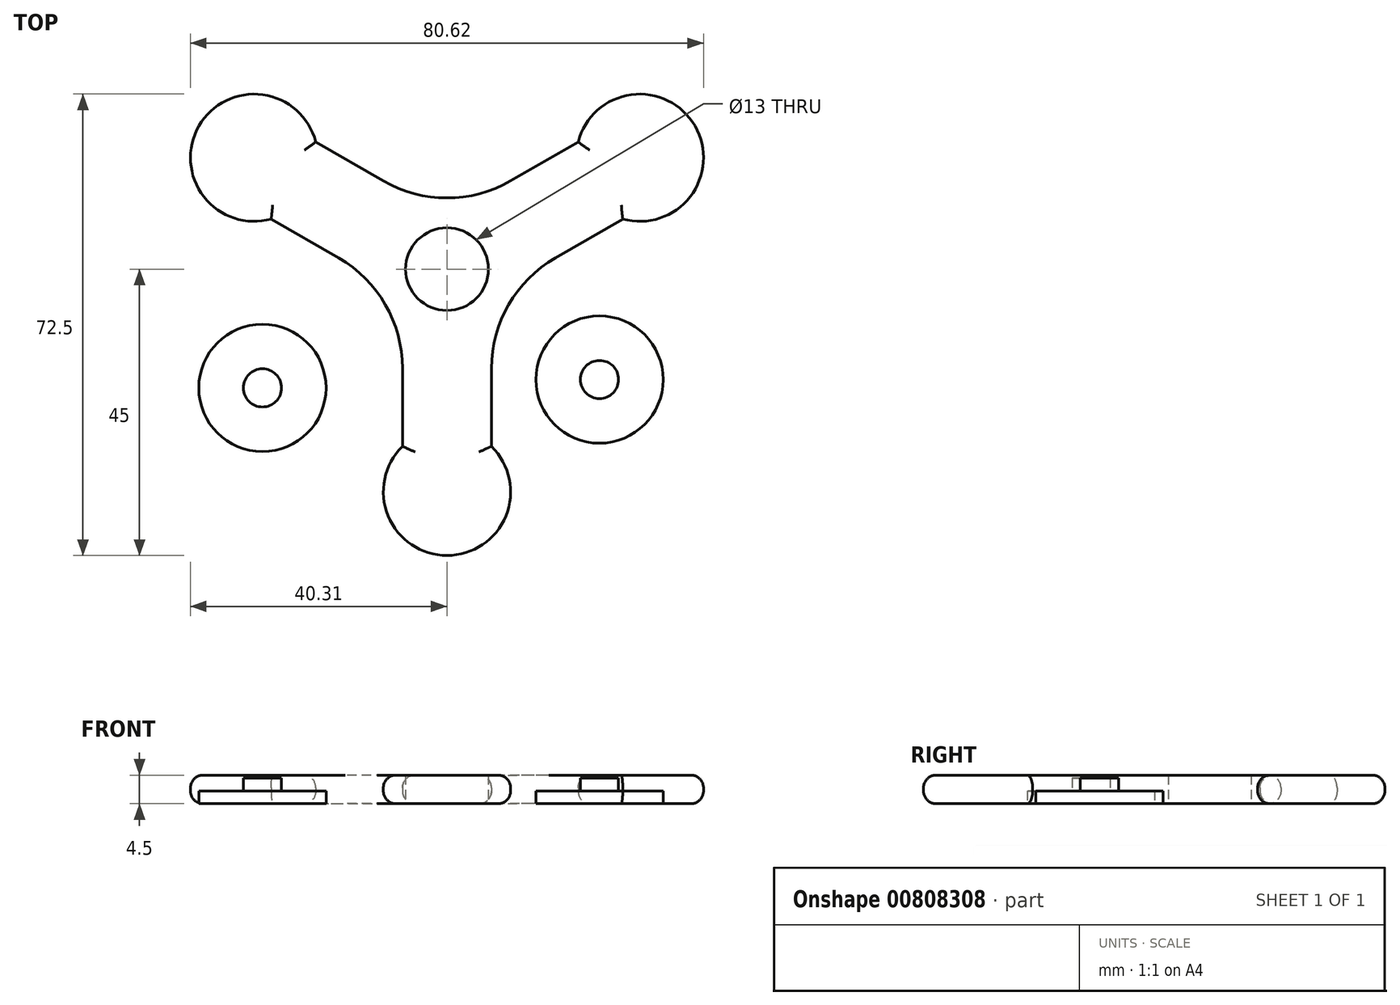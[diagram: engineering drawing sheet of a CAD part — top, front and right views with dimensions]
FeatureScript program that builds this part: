
annotation { "Feature Type Name" : "Feature", "Feature Type Description" : "" }
export const myFeature = defineFeature(function(context is Context, id is Id, definition is map)
    precondition{}
    {
        {
            var Q0;
            Q0=qCreatedBy(makeId("Top.planeOp"),FACE);
            var sketch = newSketch(context, id + "F0", { "sketchPlane" : qUnion([Q0])});
            skCircle(sketch, "E0", {"center": v(0, 0) * mm, "radius": 6.5 * mm});
            skCircle(sketch, "E1.cCircle", {"center": v(0, 0) * mm, "radius": 9.7 * mm, "construction": true});
            skLineSegment(sketch, "E1.0", {"start": v(-16.8, 9.7) * mm, "end": v(16.8, 9.7) * mm, "construction": true});
            skLineSegment(sketch, "E1.1", {"start": v(16.8, 9.7) * mm, "end": v(0, -19.4) * mm, "construction": true});
            skLineSegment(sketch, "E1.2", {"start": v(0, -19.4) * mm, "end": v(-16.8, 9.7) * mm, "construction": true});
            skPoint(sketch, "E1.0.midPoint", {"position": v(0, 9.7) * mm});
            skLineSegment(sketch, "E2", {"start": v(0, 0) * mm, "end": v(-37.72, 21.78) * mm, "construction": true});
            skLineSegment(sketch, "E3", {"start": v(0, 0) * mm, "end": v(32.3, 18.65) * mm, "construction": true});
            skLineSegment(sketch, "E4", {"start": v(0, 0) * mm, "end": v(0, -39.08) * mm, "construction": true});
            skLineSegment(sketch, "E5", {"start": v(0, 8.08) * mm, "end": v(26.1, 23.15) * mm, "construction": true});
            skLineSegment(sketch, "E6", {"start": v(-34.22, 11.67) * mm, "end": v(-7, -4.04) * mm, "construction": true});
            skLineSegment(sketch, "E7", {"start": v(-7, -4.04) * mm, "end": v(-7, -34.03) * mm, "construction": true});
            skLineSegment(sketch, "E8", {"start": v(7, -32.22) * mm, "end": v(7, -4.04) * mm, "construction": true});
            skLineSegment(sketch, "E9", {"start": v(7, -4.04) * mm, "end": v(32.17, 10.5) * mm, "construction": true});
            skLineSegment(sketch, "E10", {"start": v(0, 8.08) * mm, "end": v(-23.07, 21.4) * mm, "construction": true});
            skCircle(sketch, "E11", {"center": v(30.31, 17.5) * mm, "radius": 10 * mm});
            skCircle(sketch, "E12", {"center": v(-30.31, 17.5) * mm, "radius": 10 * mm});
            skCircle(sketch, "E13", {"center": v(0, -35) * mm, "radius": 10 * mm});
            skLineSegment(sketch, "E14", {"start": v(-27.63, 7.87) * mm, "end": v(-17, 1.73) * mm});
            skLineSegment(sketch, "E15", {"start": v(-7, -27.86) * mm, "end": v(-7, -15.59) * mm});
            skLineSegment(sketch, "E16", {"start": v(-20.63, 20) * mm, "end": v(-10, 13.86) * mm});
            skLineSegment(sketch, "E17", {"start": v(20.63, 20) * mm, "end": v(10, 13.86) * mm});
            skLineSegment(sketch, "E18", {"start": v(27.63, 7.87) * mm, "end": v(17, 1.73) * mm});
            skLineSegment(sketch, "E19", {"start": v(7, -27.86) * mm, "end": v(7, -15.59) * mm});
            skPoint(sketch, "E20.visualSharp", {"position": v(-7, -4.04) * mm});
            skArc(sketch, "E20.filletArc", {"start": v(-7, -15.59) * mm, "mid": v(-9.68, -5.59) * mm, "end": v(-17, 1.73) * mm});
            skPoint(sketch, "E21.visualSharp", {"position": v(0, 8.08) * mm});
            skArc(sketch, "E21.filletArc", {"start": v(-10, 13.86) * mm, "mid": v(0, 11.18) * mm, "end": v(10, 13.86) * mm});
            skPoint(sketch, "E22.visualSharp", {"position": v(7, -4.04) * mm});
            skArc(sketch, "E22.filletArc", {"start": v(17, 1.73) * mm, "mid": v(9.68, -5.59) * mm, "end": v(7, -15.59) * mm});
            skCircle(sketch, "E23", {"center": v(-29, -18.67) * mm, "radius": 10 * mm});
            skCircle(sketch, "E24", {"center": v(23.97, -17.36) * mm, "radius": 10 * mm});
            skSolve(sketch);
        }
        {
            var Q0;
            {var subQ0=sQuery(id+"F0.wireOp",EDGE,"E12");var subQ1=makeQuery(id+"F0.imprint","INTERSECT",VERTEX,{"derivedFrom":[subQ0,sQuery(id+"F0.wireOp",EDGE,"E14")]});Q0=makeQuery(id+"F0.imprint","IMPRINT",FACE,{"disambiguationData":[TD([[makeQuery(id+"F0.imprint","IMPRINT",EDGE,{"disambiguationData":[TD([[subQ1,1.0]])],"derivedFrom":subQ0}),1.0]])]});}
            var Q1;
            {var subQ0=sQuery(id+"F0.wireOp",EDGE,"E13");var subQ1=makeQuery(id+"F0.imprint","INTERSECT",VERTEX,{"derivedFrom":[subQ0,sQuery(id+"F0.wireOp",EDGE,"E15")]});Q1=makeQuery(id+"F0.imprint","IMPRINT",FACE,{"disambiguationData":[TD([[makeQuery(id+"F0.imprint","IMPRINT",EDGE,{"disambiguationData":[TD([[subQ1,1.0]])],"derivedFrom":subQ0}),1.0]])]});}
            var Q2;
            {var subQ0=sQuery(id+"F0.wireOp",EDGE,"E11");var subQ1=makeQuery(id+"F0.imprint","INTERSECT",VERTEX,{"derivedFrom":[subQ0,sQuery(id+"F0.wireOp",EDGE,"E17")]});Q2=makeQuery(id+"F0.imprint","IMPRINT",FACE,{"disambiguationData":[TD([[makeQuery(id+"F0.imprint","IMPRINT",EDGE,{"disambiguationData":[TD([[subQ1,-1.0]])],"derivedFrom":subQ0}),1.0]])]});}
            var Q3;
            Q3=makeQuery(id+"F0.imprint","IMPRINT",FACE,{"disambiguationData":[TD([[makeQuery(id+"F0.imprint","IMPRINT",EDGE,{"derivedFrom":sQuery(id+"F0.wireOp",EDGE,"E0")}),-1.0]])]});
            extrude(context, id + "F1", {"entities" : qUnion([Q0, Q1, Q2, Q3]), "depth" : 4.5 * mm, "offsetDistance" : 25 * mm});
        }
        {
            var Q0;
            Q0=makeQuery(id+"F1.opExtrude","CAP_EDGE",EDGE,{"disambiguationData":[OSD([sQuery(id+"F0.wireOp",EDGE,"E13")])],"isStart":false});
            var Q1;
            Q1=makeQuery(id+"F1.opExtrude","CAP_EDGE",EDGE,{"disambiguationData":[OSD([sQuery(id+"F0.wireOp",EDGE,"E19")])],"isStart":false});
            var Q2;
            Q2=makeQuery(id+"F1.opExtrude","CAP_EDGE",EDGE,{"disambiguationData":[OSD([sQuery(id+"F0.wireOp",EDGE,"E22.filletArc")])],"isStart":false});
            var Q3;
            Q3=makeQuery(id+"F1.opExtrude","CAP_EDGE",EDGE,{"disambiguationData":[OSD([sQuery(id+"F0.wireOp",EDGE,"E18")])],"isStart":false});
            var Q4;
            Q4=makeQuery(id+"F1.opExtrude","CAP_EDGE",EDGE,{"disambiguationData":[OSD([sQuery(id+"F0.wireOp",EDGE,"E11")])],"isStart":false});
            var Q5;
            Q5=makeQuery(id+"F1.opExtrude","CAP_EDGE",EDGE,{"disambiguationData":[OSD([sQuery(id+"F0.wireOp",EDGE,"E17")])],"isStart":false});
            var Q6;
            Q6=makeQuery(id+"F1.opExtrude","CAP_EDGE",EDGE,{"disambiguationData":[OSD([sQuery(id+"F0.wireOp",EDGE,"E21.filletArc")])],"isStart":false});
            var Q7;
            Q7=makeQuery(id+"F1.opExtrude","CAP_EDGE",EDGE,{"disambiguationData":[OSD([sQuery(id+"F0.wireOp",EDGE,"E16")])],"isStart":false});
            var Q8;
            Q8=makeQuery(id+"F1.opExtrude","CAP_EDGE",EDGE,{"disambiguationData":[OSD([sQuery(id+"F0.wireOp",EDGE,"E12")])],"isStart":false});
            var Q9;
            Q9=makeQuery(id+"F1.opExtrude","CAP_EDGE",EDGE,{"disambiguationData":[OSD([sQuery(id+"F0.wireOp",EDGE,"E14")])],"isStart":false});
            var Q10;
            Q10=makeQuery(id+"F1.opExtrude","CAP_EDGE",EDGE,{"disambiguationData":[OSD([sQuery(id+"F0.wireOp",EDGE,"E20.filletArc")])],"isStart":false});
            var Q11;
            Q11=makeQuery(id+"F1.opExtrude","CAP_EDGE",EDGE,{"disambiguationData":[OSD([sQuery(id+"F0.wireOp",EDGE,"E15")])],"isStart":false});
            fillet(context, id + "F2", {"entities" : qUnion([Q0, Q1, Q2, Q3, Q4, Q5, Q6, Q7, Q8, Q9, Q10, Q11]), "radius" : 2 * mm, "tangentPropagation" : true, "allowEdgeOverflow" : false});
        }
        {
            var Q0;
            Q0=makeQuery(id+"F1.opExtrude","CAP_EDGE",EDGE,{"disambiguationData":[OSD([sQuery(id+"F0.wireOp",EDGE,"E12")])],"isStart":true});
            var Q1;
            Q1=makeQuery(id+"F1.opExtrude","CAP_EDGE",EDGE,{"disambiguationData":[OSD([sQuery(id+"F0.wireOp",EDGE,"E14")])],"isStart":true});
            var Q2;
            Q2=makeQuery(id+"F1.opExtrude","CAP_EDGE",EDGE,{"disambiguationData":[OSD([sQuery(id+"F0.wireOp",EDGE,"E20.filletArc")])],"isStart":true});
            var Q3;
            Q3=makeQuery(id+"F1.opExtrude","CAP_EDGE",EDGE,{"disambiguationData":[OSD([sQuery(id+"F0.wireOp",EDGE,"E15")])],"isStart":true});
            var Q4;
            Q4=makeQuery(id+"F1.opExtrude","CAP_EDGE",EDGE,{"disambiguationData":[OSD([sQuery(id+"F0.wireOp",EDGE,"E13")])],"isStart":true});
            var Q5;
            Q5=makeQuery(id+"F1.opExtrude","CAP_EDGE",EDGE,{"disambiguationData":[OSD([sQuery(id+"F0.wireOp",EDGE,"E19")])],"isStart":true});
            var Q6;
            Q6=makeQuery(id+"F1.opExtrude","CAP_EDGE",EDGE,{"disambiguationData":[OSD([sQuery(id+"F0.wireOp",EDGE,"E22.filletArc")])],"isStart":true});
            var Q7;
            Q7=makeQuery(id+"F1.opExtrude","CAP_EDGE",EDGE,{"disambiguationData":[OSD([sQuery(id+"F0.wireOp",EDGE,"E16")])],"isStart":true});
            var Q8;
            Q8=makeQuery(id+"F1.opExtrude","CAP_EDGE",EDGE,{"disambiguationData":[OSD([sQuery(id+"F0.wireOp",EDGE,"E21.filletArc")])],"isStart":true});
            var Q9;
            Q9=makeQuery(id+"F1.opExtrude","CAP_EDGE",EDGE,{"disambiguationData":[OSD([sQuery(id+"F0.wireOp",EDGE,"E17")])],"isStart":true});
            var Q10;
            Q10=makeQuery(id+"F1.opExtrude","CAP_EDGE",EDGE,{"disambiguationData":[OSD([sQuery(id+"F0.wireOp",EDGE,"E18")])],"isStart":true});
            var Q11;
            Q11=makeQuery(id+"F1.opExtrude","CAP_EDGE",EDGE,{"disambiguationData":[OSD([sQuery(id+"F0.wireOp",EDGE,"E11")])],"isStart":true});
            fillet(context, id + "F3", {"entities" : qUnion([Q0, Q1, Q2, Q3, Q4, Q5, Q6, Q7, Q8, Q9, Q10, Q11]), "radius" : 2 * mm, "tangentPropagation" : true, "allowEdgeOverflow" : false});
        }
        {
            var Q0;
            Q0=makeQuery(id+"F0.imprint","IMPRINT",FACE,{"disambiguationData":[TD([[makeQuery(id+"F0.imprint","IMPRINT",EDGE,{"derivedFrom":sQuery(id+"F0.wireOp",EDGE,"E23")}),1.0]])]});
            var Q1;
            Q1=makeQuery(id+"F0.imprint","IMPRINT",FACE,{"disambiguationData":[TD([[makeQuery(id+"F0.imprint","IMPRINT",EDGE,{"derivedFrom":sQuery(id+"F0.wireOp",EDGE,"E24")}),1.0]])]});
            extrude(context, id + "F4", {"entities" : qUnion([Q0, Q1]), "depth" : 2 * mm, "offsetDistance" : 25 * mm});
        }
        {
            var Q0;
            Q0=makeQuery(id+"F4.opExtrude","CAP_FACE",FACE,{"disambiguationData":[OSD([sQuery(id+"F0.wireOp",EDGE,"E23")])],"isStart":false});
            var sketch = newSketch(context, id + "F5", { "sketchPlane" : qUnion([Q0])});
            skCircle(sketch, "E25", {"center": v(-29, -18.67) * mm, "radius": 3 * mm});
            skSolve(sketch);
        }
        {
            var Q0;
            Q0=makeQuery(id+"F5.imprint","IMPRINT",FACE,{"disambiguationData":[TD([[makeQuery(id+"F5.imprint","IMPRINT",EDGE,{"derivedFrom":sQuery(id+"F5.wireOp",EDGE,"E25")}),1.0]])]});
            extrude(context, id + "F6", {"entities" : qUnion([Q0]), "operationType" : NewBodyOperationType.ADD, "depth" : 2 * mm, "offsetDistance" : 25 * mm});
        }
        {
            var Q0;
            Q0=makeQuery(id+"F4.opExtrude","CAP_FACE",FACE,{"disambiguationData":[OSD([sQuery(id+"F0.wireOp",EDGE,"E24")])],"isStart":false});
            var sketch = newSketch(context, id + "F7", { "sketchPlane" : qUnion([Q0])});
            skCircle(sketch, "E26", {"center": v(23.97, -17.36) * mm, "radius": 3 * mm});
            skSolve(sketch);
        }
        {
            var Q0;
            Q0=makeQuery(id+"F7.imprint","IMPRINT",FACE,{"disambiguationData":[TD([[makeQuery(id+"F7.imprint","IMPRINT",EDGE,{"derivedFrom":sQuery(id+"F7.wireOp",EDGE,"E26")}),1.0]])]});
            extrude(context, id + "F8", {"entities" : qUnion([Q0]), "operationType" : NewBodyOperationType.ADD, "depth" : 2 * mm, "offsetDistance" : 25 * mm});
        }
    });
